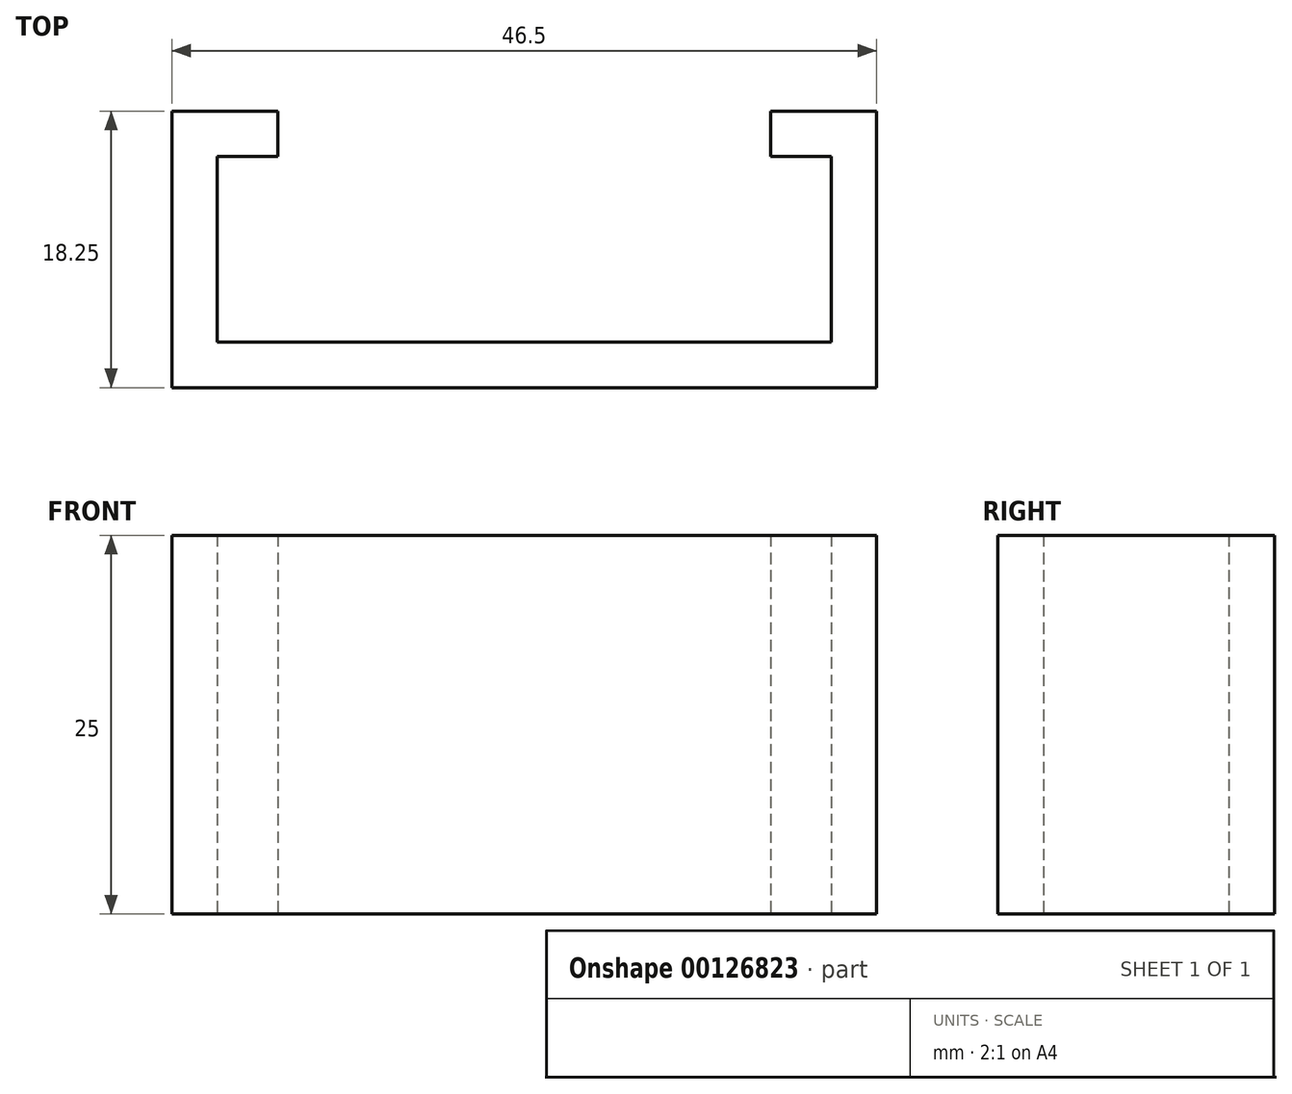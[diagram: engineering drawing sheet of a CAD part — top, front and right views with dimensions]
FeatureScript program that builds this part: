
annotation { "Feature Type Name" : "Feature", "Feature Type Description" : "" }
export const myFeature = defineFeature(function(context is Context, id is Id, definition is map)
    precondition{}
    {
        {
            var Q0;
            Q0=qCreatedBy(makeId("Top.planeOp"),FACE);
            var sketch = newSketch(context, id + "F0", { "sketchPlane" : qUnion([Q0])});
            skLineSegment(sketch, "E0.bottom", {"start": v(0, 0) * mm, "end": v(40.5, 0) * mm});
            skLineSegment(sketch, "E0.top", {"start": v(0, 12.25) * mm, "end": v(4, 12.25) * mm});
            skLineSegment(sketch, "E0.left", {"start": v(0, 0) * mm, "end": v(0, 12.25) * mm});
            skLineSegment(sketch, "E0.right", {"start": v(40.5, 0) * mm, "end": v(40.5, 12.25) * mm});
            skLineSegment(sketch, "E1.0", {"start": v(43.5, -3) * mm, "end": v(43.5, 15.25) * mm});
            skLineSegment(sketch, "E1.1", {"start": v(-3, -3) * mm, "end": v(43.5, -3) * mm});
            skLineSegment(sketch, "E1.2", {"start": v(-3, -3) * mm, "end": v(-3, 15.25) * mm});
            skLineSegment(sketch, "E1.3", {"start": v(-3, 15.25) * mm, "end": v(4, 15.25) * mm});
            skLineSegment(sketch, "E2", {"start": v(4, 15.25) * mm, "end": v(4, 12.25) * mm});
            skLineSegment(sketch, "E3", {"start": v(36.5, 12.25) * mm, "end": v(36.5, 15.25) * mm});
            skLineSegment(sketch, "E4.trimOffspring", {"start": v(36.5, 12.25) * mm, "end": v(40.5, 12.25) * mm});
            skLineSegment(sketch, "E5.trimOffspring", {"start": v(36.5, 15.25) * mm, "end": v(43.5, 15.25) * mm});
            skSolve(sketch);
        }
        {
            var Q0;
            Q0=makeQuery(id+"F0.imprint","IMPRINT",FACE,{"disambiguationData":[TD([[makeQuery(id+"F0.imprint","IMPRINT",EDGE,{"derivedFrom":sQuery(id+"F0.wireOp",EDGE,"E0.bottom")}),-1.0]])]});
            extrude(context, id + "F1", {"entities" : qUnion([Q0]), "depth" : 25 * mm});
        }
    });
